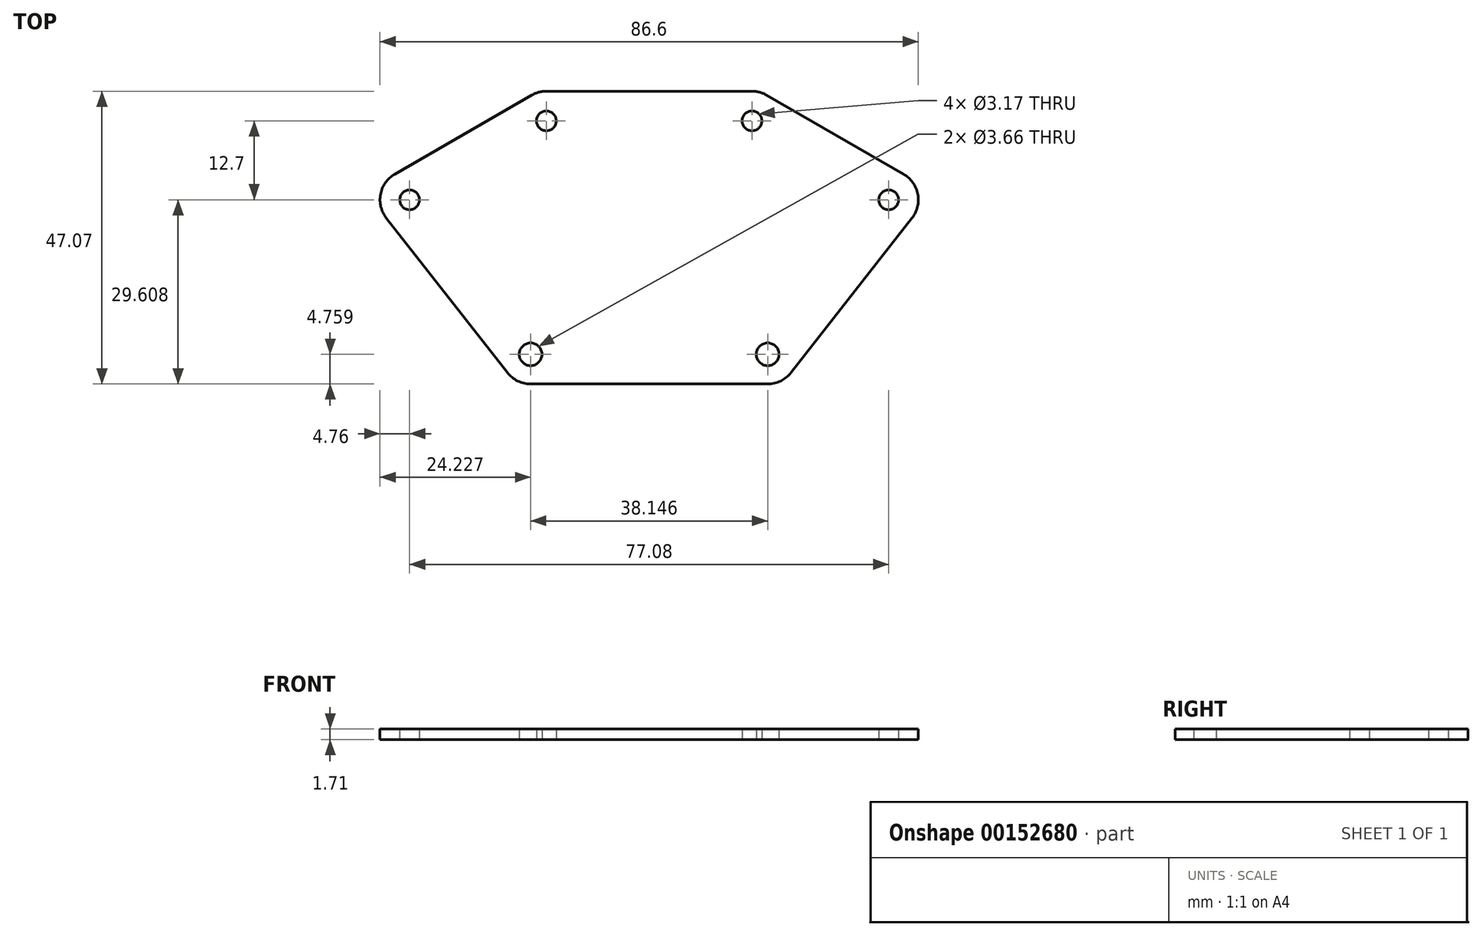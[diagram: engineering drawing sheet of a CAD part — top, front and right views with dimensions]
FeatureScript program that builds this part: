
annotation { "Feature Type Name" : "Feature", "Feature Type Description" : "" }
export const myFeature = defineFeature(function(context is Context, id is Id, definition is map)
    precondition{}
    {
        {
            var Q0;
            Q0=qCreatedBy(makeId("Top.planeOp"),FACE);
            var sketch = newSketch(context, id + "F0", { "sketchPlane" : qUnion([Q0])});
            skLineSegment(sketch, "E0.top", {"start": v(20.32, -9.78) * mm, "end": v(-20.32, -9.78) * mm, "construction": true});
            skLineSegment(sketch, "E1.top", {"start": v(20.32, 9.78) * mm, "end": v(-20.32, 9.78) * mm, "construction": true});
            skLineSegment(sketch, "E2", {"start": v(0, -9.78) * mm, "end": v(0, 9.78) * mm, "construction": true});
            skPoint(sketch, "E3.middle", {"position": v(0, 0) * mm});
            skLineSegment(sketch, "E4", {"start": v(0, 9.78) * mm, "end": v(0, 23) * mm, "construction": true});
            skLineSegment(sketch, "E5", {"start": v(-16.54, 23) * mm, "end": v(16.54, 23) * mm, "construction": true});
            skLineSegment(sketch, "E6", {"start": v(16.54, 23) * mm, "end": v(38.54, 10.3) * mm, "construction": true});
            skLineSegment(sketch, "E7", {"start": v(-16.54, 23) * mm, "end": v(-38.54, 10.3) * mm, "construction": true});
            skCircle(sketch, "E8", {"center": v(38.54, 10.3) * mm, "radius": 1.59 * mm});
            skCircle(sketch, "E9", {"center": v(16.54, 23) * mm, "radius": 1.59 * mm});
            skCircle(sketch, "E10", {"center": v(-16.54, 23) * mm, "radius": 1.59 * mm});
            skCircle(sketch, "E11", {"center": v(-38.54, 10.3) * mm, "radius": 1.59 * mm});
            skLineSegment(sketch, "E12", {"start": v(0, 23) * mm, "end": v(0, 27.77) * mm, "construction": true});
            skLineSegment(sketch, "E13", {"start": v(38.54, 10.3) * mm, "end": v(0, 10.3) * mm, "construction": true});
            skLineSegment(sketch, "E14", {"start": v(0, 10.3) * mm, "end": v(-38.54, 10.3) * mm, "construction": true});
            skLineSegment(sketch, "E15", {"start": v(-16.54, 27.77) * mm, "end": v(16.54, 27.77) * mm});
            skArc(sketch, "E16", {"start": v(42.29, 7.37) * mm, "mid": v(43.22, 11.21) * mm, "end": v(40.92, 14.43) * mm});
            skArc(sketch, "E17", {"start": v(18.92, 27.13) * mm, "mid": v(17.78, 27.6) * mm, "end": v(16.54, 27.77) * mm});
            skArc(sketch, "E18", {"start": v(-16.54, 27.77) * mm, "mid": v(-17.78, 27.6) * mm, "end": v(-18.92, 27.13) * mm});
            skArc(sketch, "E19", {"start": v(-40.92, 14.43) * mm, "mid": v(-43.22, 11.21) * mm, "end": v(-42.29, 7.37) * mm});
            skLineSegment(sketch, "E20", {"start": v(18.92, 27.13) * mm, "end": v(40.92, 14.43) * mm});
            skLineSegment(sketch, "E21", {"start": v(-18.92, 27.13) * mm, "end": v(-40.92, 14.43) * mm});
            skLineSegment(sketch, "E22", {"start": v(-42.29, 7.37) * mm, "end": v(-22.82, -17.48) * mm});
            skLineSegment(sketch, "E23", {"start": v(42.29, 7.37) * mm, "end": v(22.82, -17.48) * mm});
            skArc(sketch, "E24", {"start": v(-22.82, -17.48) * mm, "mid": v(-21.16, -18.82) * mm, "end": v(-19.07, -19.3) * mm});
            skArc(sketch, "E25", {"start": v(19.07, -19.3) * mm, "mid": v(21.16, -18.82) * mm, "end": v(22.82, -17.48) * mm});
            skLineSegment(sketch, "E26", {"start": v(0, -9.78) * mm, "end": v(0, -14.54) * mm, "construction": true});
            skLineSegment(sketch, "E27", {"start": v(-19.07, -14.54) * mm, "end": v(19.07, -14.54) * mm, "construction": true});
            skLineSegment(sketch, "E28", {"start": v(0, -14.54) * mm, "end": v(0, -19.3) * mm, "construction": true});
            skLineSegment(sketch, "E29", {"start": v(-19.07, -19.3) * mm, "end": v(19.07, -19.3) * mm});
            skCircle(sketch, "E30", {"center": v(-19.07, -14.54) * mm, "radius": 1.83 * mm});
            skCircle(sketch, "E31", {"center": v(19.07, -14.54) * mm, "radius": 1.83 * mm});
            skLineSegment(sketch, "E32", {"start": v(-20.32, -9.78) * mm, "end": v(-20.32, 9.78) * mm, "construction": true});
            skLineSegment(sketch, "E33", {"start": v(20.32, -9.78) * mm, "end": v(20.32, 9.78) * mm, "construction": true});
            skLineSegment(sketch, "E34", {"start": v(-20.32, 0) * mm, "end": v(-10.9, 0) * mm, "construction": true});
            skLineSegment(sketch, "E35", {"start": v(-10.9, 0) * mm, "end": v(-16.54, 23) * mm, "construction": true});
            skSolve(sketch);
        }
        {
            var Q0;
            Q0=qSketchRegion(id+"F0",true);
            extrude(context, id + "F1", {"entities" : qUnion([Q0]), "depth" : 1.7 * mm});
        }
    });
